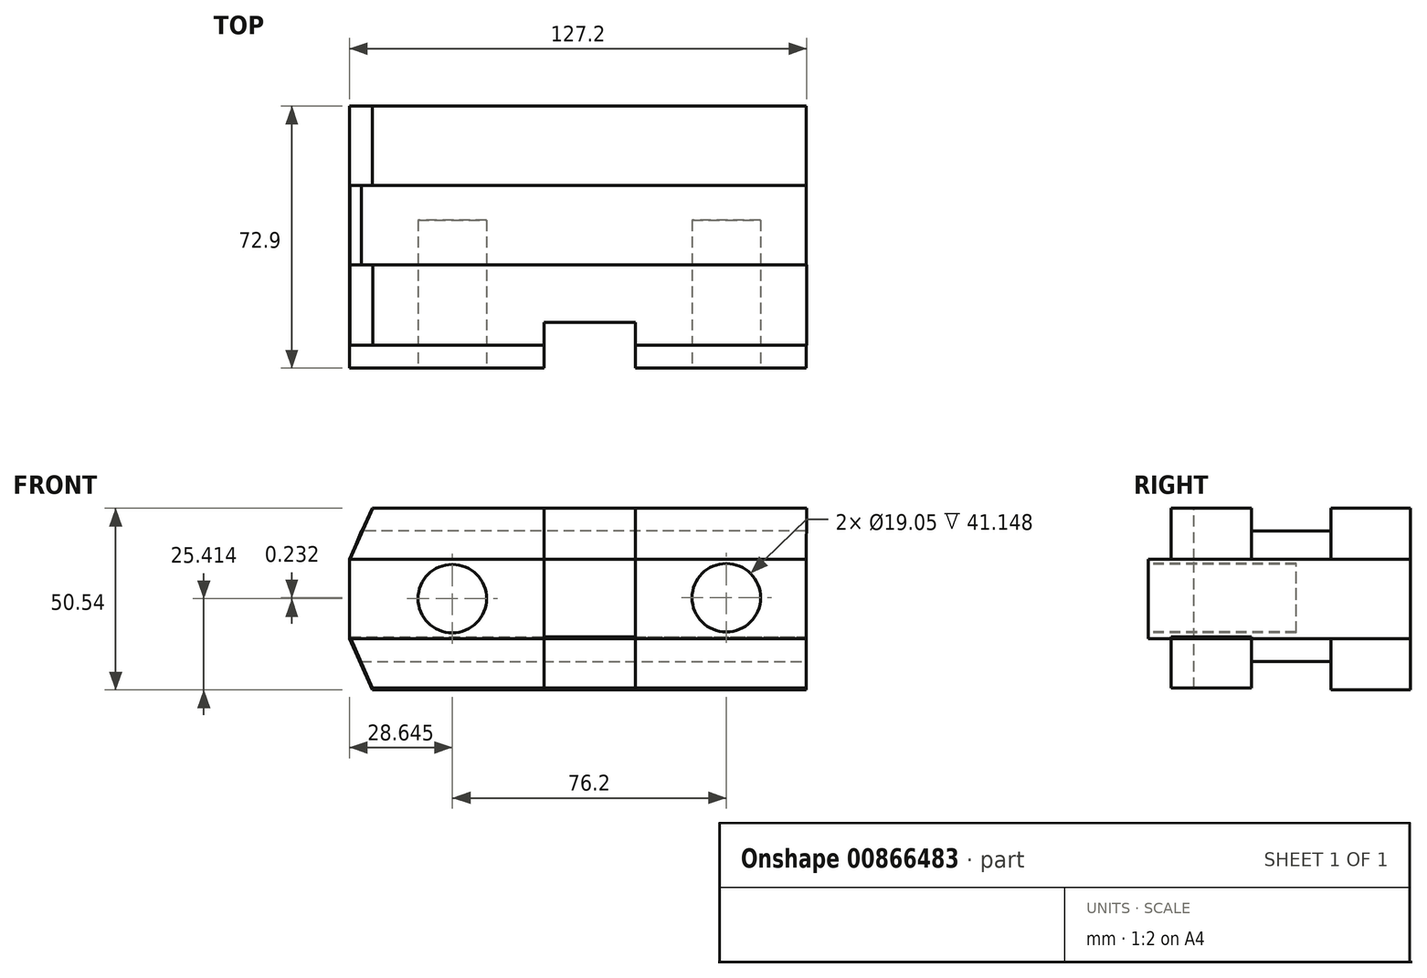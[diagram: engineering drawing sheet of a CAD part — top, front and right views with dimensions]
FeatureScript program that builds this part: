
annotation { "Feature Type Name" : "Feature", "Feature Type Description" : "" }
export const myFeature = defineFeature(function(context is Context, id is Id, definition is map)
    precondition{}
    {
        {
            var Q0;
            Q0=qCreatedBy(makeId("Front.planeOp"),FACE);
            var sketch = newSketch(context, id + "F0", { "sketchPlane" : qUnion([Q0])});
            skLineSegment(sketch, "E0", {"start": v(0, 0) * mm, "end": v(-47.5, 0) * mm});
            skLineSegment(sketch, "E1", {"start": v(0, 0) * mm, "end": v(0, -22.1) * mm});
            skLineSegment(sketch, "E2", {"start": v(0, -22.1) * mm, "end": v(-47.5, -22.1) * mm});
            skLineSegment(sketch, "E3", {"start": v(-127, 0) * mm, "end": v(-127, -22.1) * mm});
            skLineSegment(sketch, "E4", {"start": v(-70.52, -22.1) * mm, "end": v(-127, -22.1) * mm});
            skLineSegment(sketch, "E5.trimOffspring", {"start": v(-70.52, 0) * mm, "end": v(-127, 0) * mm});
            skLineSegment(sketch, "E6", {"start": v(0, -22.1) * mm, "end": v(0, -36.32) * mm});
            skLineSegment(sketch, "E7", {"start": v(0, -36.32) * mm, "end": v(-47.5, -36.32) * mm});
            skLineSegment(sketch, "E8", {"start": v(-70.52, -36.32) * mm, "end": v(-120.65, -36.32) * mm});
            skLineSegment(sketch, "E9", {"start": v(-127, -22.1) * mm, "end": v(-120.65, -36.32) * mm});
            skLineSegment(sketch, "E10", {"start": v(0, 0) * mm, "end": v(0, 14.22) * mm});
            skLineSegment(sketch, "E11", {"start": v(-47.5, 14.22) * mm, "end": v(0, 14.22) * mm});
            skLineSegment(sketch, "E12", {"start": v(-70.52, 14.22) * mm, "end": v(-120.65, 14.22) * mm});
            skLineSegment(sketch, "E13", {"start": v(-127, 0) * mm, "end": v(-120.65, 14.22) * mm});
            skLineSegment(sketch, "E14", {"start": v(-70.52, -22.1) * mm, "end": v(-47.5, -22.1) * mm});
            skLineSegment(sketch, "E15", {"start": v(-70.52, 0) * mm, "end": v(-47.5, 0) * mm});
            skLineSegment(sketch, "E16", {"start": v(-70.52, 14.22) * mm, "end": v(-47.5, 14.22) * mm});
            skLineSegment(sketch, "E17", {"start": v(-70.52, -36.32) * mm, "end": v(-47.5, -36.32) * mm});
            skSolve(sketch);
        }
        {
            var Q0;
            Q0=makeQuery(id+"F0.imprint","IMPRINT",FACE,{"disambiguationData":[TD([[makeQuery(id+"F0.imprint","IMPRINT",EDGE,{"derivedFrom":sQuery(id+"F0.wireOp",EDGE,"E0")}),-1.0]])]});
            var Q1;
            Q1=makeQuery(id+"F0.imprint","IMPRINT",FACE,{"disambiguationData":[TD([[makeQuery(id+"F0.imprint","IMPRINT",EDGE,{"derivedFrom":sQuery(id+"F0.wireOp",EDGE,"E2")}),1.0]])]});
            extrude(context, id + "F1", {"entities" : qUnion([Q0, Q1]), "depth" : 22.1 * mm, "offsetDistance" : 25.4 * mm});
        }
        {
            var Q0;
            Q0=makeQuery(id+"F1.opExtrude","CAP_FACE",FACE,{"disambiguationData":[OSD([sQuery(id+"F0.wireOp",EDGE,"E2"),sQuery(id+"F0.wireOp",EDGE,"E4"),sQuery(id+"F0.wireOp",EDGE,"E6"),sQuery(id+"F0.wireOp",EDGE,"E7"),sQuery(id+"F0.wireOp",EDGE,"E8"),sQuery(id+"F0.wireOp",EDGE,"E9"),sQuery(id+"F0.wireOp",EDGE,"E14"),sQuery(id+"F0.wireOp",EDGE,"E17")])],"isStart":false});
            var sketch = newSketch(context, id + "F2", { "sketchPlane" : qUnion([Q0])});
            skPoint(sketch, "E18.start.orphan", {"position": v(-123.82, -28.45) * mm});
            skLineSegment(sketch, "E19", {"start": v(-123.82, -28.45) * mm, "end": v(0, -28.45) * mm});
            skLineSegment(sketch, "E20", {"start": v(0, 7.87) * mm, "end": v(-35.51, 7.87) * mm});
            skLineSegment(sketch, "E21", {"start": v(-35.51, 7.87) * mm, "end": v(-123.58, 7.87) * mm});
            skLineSegment(sketch, "E22", {"start": v(-123.82, -28.45) * mm, "end": v(-127, -22.1) * mm});
            skLineSegment(sketch, "E23", {"start": v(-127, -22.1) * mm, "end": v(0, -22.1) * mm});
            skLineSegment(sketch, "E24", {"start": v(0, -22.1) * mm, "end": v(0, -28.45) * mm});
            skLineSegment(sketch, "E25", {"start": v(0, 7.87) * mm, "end": v(0, 0) * mm});
            skLineSegment(sketch, "E26", {"start": v(0, 0) * mm, "end": v(-126.8, 0) * mm});
            skLineSegment(sketch, "E27", {"start": v(-126.8, 0) * mm, "end": v(-123.58, 7.87) * mm});
            skSolve(sketch);
        }
        {
            var Q0;
            Q0 = qSketchRegion(id + "F2", true);
            extrude(context, id + "F3", {"entities" : qUnion([Q0]), "depth" : 22.1 * mm, "offsetDistance" : 25.4 * mm});
        }
        {
            var Q0;
            Q0=makeQuery(id+"F3.opExtrude","CAP_FACE",FACE,{"disambiguationData":[OSD([sQuery(id+"F2.wireOp",EDGE,"E20"),sQuery(id+"F2.wireOp",EDGE,"E21"),sQuery(id+"F2.wireOp",EDGE,"E25"),sQuery(id+"F2.wireOp",EDGE,"E26"),sQuery(id+"F2.wireOp",EDGE,"E27")])],"isStart":false});
            var sketch = newSketch(context, id + "F4", { "sketchPlane" : qUnion([Q0])});
            skLineSegment(sketch, "E28", {"start": v(-126.8, 0) * mm, "end": v(-120.45, 14.22) * mm});
            skLineSegment(sketch, "E29", {"start": v(-120.45, 14.22) * mm, "end": v(0.2, 14.22) * mm});
            skLineSegment(sketch, "E30", {"start": v(0.2, 14.22) * mm, "end": v(0, 0) * mm});
            skLineSegment(sketch, "E31", {"start": v(0, 0) * mm, "end": v(-126.8, 0) * mm});
            skLineSegment(sketch, "E32", {"start": v(-126.8, -21.6) * mm, "end": v(0, -21.6) * mm});
            skLineSegment(sketch, "E33", {"start": v(0, -21.6) * mm, "end": v(0, -35.82) * mm});
            skLineSegment(sketch, "E34", {"start": v(0, -35.82) * mm, "end": v(-120.65, -35.82) * mm});
            skLineSegment(sketch, "E35", {"start": v(-120.65, -35.82) * mm, "end": v(-126.8, -21.6) * mm});
            skSolve(sketch);
        }
        {
            var Q0;
            Q0 = qSketchRegion(id + "F4", true);
            extrude(context, id + "F5", {"entities" : qUnion([Q0]), "depth" : 22.35 * mm, "offsetDistance" : 25.4 * mm});
        }
        {
            var Q0;
            Q0=makeQuery(id+"F0.imprint","IMPRINT",FACE,{"disambiguationData":[TD([[makeQuery(id+"F0.imprint","IMPRINT",EDGE,{"derivedFrom":sQuery(id+"F0.wireOp",EDGE,"E0")}),1.0]])]});
            extrude(context, id + "F6", {"entities" : qUnion([Q0]), "depth" : 72.9 * mm, "offsetDistance" : 25.4 * mm});
        }
        {
            var Q0;
            Q0=makeQuery(id+"F5.opExtrude","CAP_FACE",FACE,{"disambiguationData":[OSD([sQuery(id+"F4.wireOp",EDGE,"E32"),sQuery(id+"F4.wireOp",EDGE,"E33"),sQuery(id+"F4.wireOp",EDGE,"E34"),sQuery(id+"F4.wireOp",EDGE,"E35")])],"isStart":false});
            var sketch = newSketch(context, id + "F7", { "sketchPlane" : qUnion([Q0])});
            skLineSegment(sketch, "E36", {"start": v(-72.9, -21.6) * mm, "end": v(-72.9, -35.82) * mm});
            skLineSegment(sketch, "E37", {"start": v(-72.9, -35.82) * mm, "end": v(-47.5, -35.82) * mm});
            skLineSegment(sketch, "E38", {"start": v(-47.5, -35.82) * mm, "end": v(-47.5, -21.6) * mm});
            skLineSegment(sketch, "E39", {"start": v(-47.5, -21.6) * mm, "end": v(-72.9, -21.6) * mm});
            skLineSegment(sketch, "E40", {"start": v(-47.5, -35.82) * mm, "end": v(0, -35.82) * mm});
            skLineSegment(sketch, "E41", {"start": v(0, -35.82) * mm, "end": v(-47.5, -35.82) * mm});
            skLineSegment(sketch, "E42", {"start": v(0, -35.82) * mm, "end": v(0, -21.6) * mm});
            skLineSegment(sketch, "E43", {"start": v(0, -21.6) * mm, "end": v(-47.5, -21.6) * mm});
            skLineSegment(sketch, "E44", {"start": v(-72.9, 0) * mm, "end": v(-72.9, 14.22) * mm});
            skLineSegment(sketch, "E45", {"start": v(-47.5, 0) * mm, "end": v(-47.5, 14.29) * mm});
            skLineSegment(sketch, "E46", {"start": v(-47.5, 14.22) * mm, "end": v(-72.9, 14.22) * mm});
            skLineSegment(sketch, "E47", {"start": v(-72.9, 0) * mm, "end": v(-47.5, 0) * mm});
            skLineSegment(sketch, "E48", {"start": v(-72.9, 0) * mm, "end": v(-72.9, -21.6) * mm});
            skLineSegment(sketch, "E49", {"start": v(-47.5, 0) * mm, "end": v(-47.5, -21.6) * mm});
            skSolve(sketch);
        }
        {
            var Q0;
            Q0=makeQuery(id+"F7.imprint","IMPRINT",FACE,{"disambiguationData":[TD([[makeQuery(id+"F7.imprint","IMPRINT",EDGE,{"derivedFrom":sQuery(id+"F7.wireOp",EDGE,"E44")}),-1.0]])]});
            var Q1;
            Q1=makeQuery(id+"F7.imprint","IMPRINT",FACE,{"disambiguationData":[TD([[makeQuery(id+"F7.imprint","IMPRINT",EDGE,{"derivedFrom":sQuery(id+"F7.wireOp",EDGE,"E39")}),1.0]])]});
            var Q2;
            Q2=makeQuery(id+"F7.imprint","IMPRINT",FACE,{"disambiguationData":[TD([[makeQuery(id+"F7.imprint","IMPRINT",EDGE,{"derivedFrom":sQuery(id+"F7.wireOp",EDGE,"E36")}),1.0]])]});
            extrude(context, id + "F8", {"entities" : qUnion([Q0, Q1, Q2]), "operationType" : NewBodyOperationType.REMOVE, "oppositeDirection" : true, "depth" : 6.35 * mm, "offsetDistance" : 25.4 * mm});
        }
        {
            var Q0;
            Q0=makeQuery(id+"F6.opExtrude","CAP_FACE",FACE,{"disambiguationData":[OSD([sQuery(id+"F0.wireOp",EDGE,"E0"),sQuery(id+"F0.wireOp",EDGE,"E1"),sQuery(id+"F0.wireOp",EDGE,"E2"),sQuery(id+"F0.wireOp",EDGE,"E3"),sQuery(id+"F0.wireOp",EDGE,"E4"),sQuery(id+"F0.wireOp",EDGE,"E5.trimOffspring"),sQuery(id+"F0.wireOp",EDGE,"E14"),sQuery(id+"F0.wireOp",EDGE,"E15")])],"isStart":false});
            var sketch = newSketch(context, id + "F9", { "sketchPlane" : qUnion([Q0])});
            skLineSegment(sketch, "E50", {"start": v(0, -22.1) * mm, "end": v(-47.5, -22.1) * mm});
            skLineSegment(sketch, "E51", {"start": v(-47.5, -22.1) * mm, "end": v(-72.9, -22.1) * mm});
            skLineSegment(sketch, "E52", {"start": v(-72.9, -22.1) * mm, "end": v(-72.9, 0) * mm});
            skLineSegment(sketch, "E53", {"start": v(-72.9, 0) * mm, "end": v(-47.5, 0) * mm});
            skLineSegment(sketch, "E54", {"start": v(-47.5, 0) * mm, "end": v(-47.5, -22.1) * mm});
            skSolve(sketch);
        }
        {
            var Q0;
            Q0 = qSketchRegion(id + "F9", true);
            extrude(context, id + "F10", {"entities" : qUnion([Q0]), "operationType" : NewBodyOperationType.REMOVE, "oppositeDirection" : true, "depth" : 6.35 * mm, "offsetDistance" : 25.4 * mm});
        }
        {
            var Q0;
            {var subQ0=sQuery(id+"F4.wireOp",EDGE,"E32");var subQ1=sQuery(id+"F4.wireOp",EDGE,"E35");var subQ2=sQuery(id+"F4.wireOp",EDGE,"E34");Q0=makeQuery(id+"F8.boolean.opBoolean","SPLIT",FACE,{"disambiguationData":[TD([makeQuery(id+"F5.opExtrude","SWEPT_FACE",FACE,{"disambiguationData":[OSD([subQ1])]})])],"derivedFrom":makeQuery(id+"F5.opExtrude","CAP_FACE",FACE,{"disambiguationData":[OSD([subQ0,sQuery(id+"F4.wireOp",EDGE,"E33"),subQ2,subQ1])],"isStart":false})});}
            var sketch = newSketch(context, id + "F11", { "sketchPlane" : qUnion([Q0])});
            skLineSegment(sketch, "E55", {"start": v(-72.9, -21.6) * mm, "end": v(-72.9, -35.82) * mm});
            skLineSegment(sketch, "E56", {"start": v(-72.9, -35.82) * mm, "end": v(-120.65, -35.82) * mm});
            skLineSegment(sketch, "E57", {"start": v(-120.65, -35.82) * mm, "end": v(-126.6, -22.09) * mm});
            skLineSegment(sketch, "E58", {"start": v(-126.6, -22.09) * mm, "end": v(-72.9, -21.6) * mm});
            skSolve(sketch);
        }
        {
            var Q0;
            {var subQ0=sQuery(id+"F4.wireOp",EDGE,"E28");var subQ1=sQuery(id+"F4.wireOp",EDGE,"E31");var subQ2=sQuery(id+"F4.wireOp",EDGE,"E29");Q0=makeQuery(id+"F8.boolean.opBoolean","SPLIT",FACE,{"disambiguationData":[TD([makeQuery(id+"F5.opExtrude","SWEPT_FACE",FACE,{"disambiguationData":[OSD([subQ0])]})])],"derivedFrom":makeQuery(id+"F5.opExtrude","CAP_FACE",FACE,{"disambiguationData":[OSD([subQ0,subQ2,sQuery(id+"F4.wireOp",EDGE,"E30"),subQ1])],"isStart":false})});}
            var sketch = newSketch(context, id + "F12", { "sketchPlane" : qUnion([Q0])});
            skLineSegment(sketch, "E59", {"start": v(-72.9, 14.22) * mm, "end": v(-72.9, 0) * mm});
            skLineSegment(sketch, "E60", {"start": v(-72.9, 0) * mm, "end": v(-126.8, 0) * mm});
            skLineSegment(sketch, "E61", {"start": v(-126.8, 0) * mm, "end": v(-120.45, 14.22) * mm});
            skLineSegment(sketch, "E62", {"start": v(-120.45, 14.22) * mm, "end": v(-72.9, 14.22) * mm});
            skSolve(sketch);
        }
        {
            var Q0;
            {var subQ0=sQuery(id+"F4.wireOp",EDGE,"E32");var subQ1=sQuery(id+"F4.wireOp",EDGE,"E33");var subQ2=sQuery(id+"F4.wireOp",EDGE,"E34");Q0=makeQuery(id+"F8.boolean.opBoolean","SPLIT",FACE,{"disambiguationData":[TD([makeQuery(id+"F5.opExtrude","SWEPT_FACE",FACE,{"disambiguationData":[OSD([subQ1])]})])],"derivedFrom":makeQuery(id+"F5.opExtrude","CAP_FACE",FACE,{"disambiguationData":[OSD([subQ0,subQ1,subQ2,sQuery(id+"F4.wireOp",EDGE,"E35")])],"isStart":false})});}
            var sketch = newSketch(context, id + "F13", { "sketchPlane" : qUnion([Q0])});
            skLineSegment(sketch, "E63", {"start": v(-47.5, -21.6) * mm, "end": v(0, -21.6) * mm});
            skLineSegment(sketch, "E64", {"start": v(0, -21.6) * mm, "end": v(0, -35.82) * mm});
            skLineSegment(sketch, "E65", {"start": v(0, -35.82) * mm, "end": v(-47.5, -35.82) * mm});
            skLineSegment(sketch, "E66", {"start": v(-47.5, -35.82) * mm, "end": v(-47.5, -21.6) * mm});
            skSolve(sketch);
        }
        {
            var Q0;
            {var subQ0=sQuery(id+"F0.wireOp",EDGE,"E15");var subQ1=sQuery(id+"F0.wireOp",EDGE,"E5.trimOffspring");var subQ2=sQuery(id+"F0.wireOp",EDGE,"E0");var subQ4=sQuery(id+"F0.wireOp",EDGE,"E14");var subQ5=sQuery(id+"F0.wireOp",EDGE,"E4");var subQ6=sQuery(id+"F0.wireOp",EDGE,"E2");var subQ16=sQuery(id+"F0.wireOp",EDGE,"E3");Q0=makeQuery(id+"F10.boolean.opBoolean","SPLIT",FACE,{"disambiguationData":[TD([makeQuery(id+"F6.opExtrude","SWEPT_FACE",FACE,{"disambiguationData":[OSD([subQ16])]})])],"derivedFrom":makeQuery(id+"F6.opExtrude","CAP_FACE",FACE,{"disambiguationData":[OSD([subQ2,sQuery(id+"F0.wireOp",EDGE,"E1"),subQ6,subQ16,subQ5,subQ1,subQ4,subQ0])],"isStart":false})});}
            var sketch = newSketch(context, id + "F14", { "sketchPlane" : qUnion([Q0])});
            skCircle(sketch, "E67", {"center": v(-98.36, -10.9) * mm, "radius": 9.53 * mm});
            skCircle(sketch, "E68", {"center": v(-22.16, -10.67) * mm, "radius": 9.53 * mm});
            skSolve(sketch);
        }
        {
            var Q0;
            Q0 = qSketchRegion(id + "F14", true);
            extrude(context, id + "F15", {"entities" : qUnion([Q0]), "operationType" : NewBodyOperationType.REMOVE, "oppositeDirection" : true, "depth" : 41.15 * mm, "offsetDistance" : 25.4 * mm});
        }
    });
